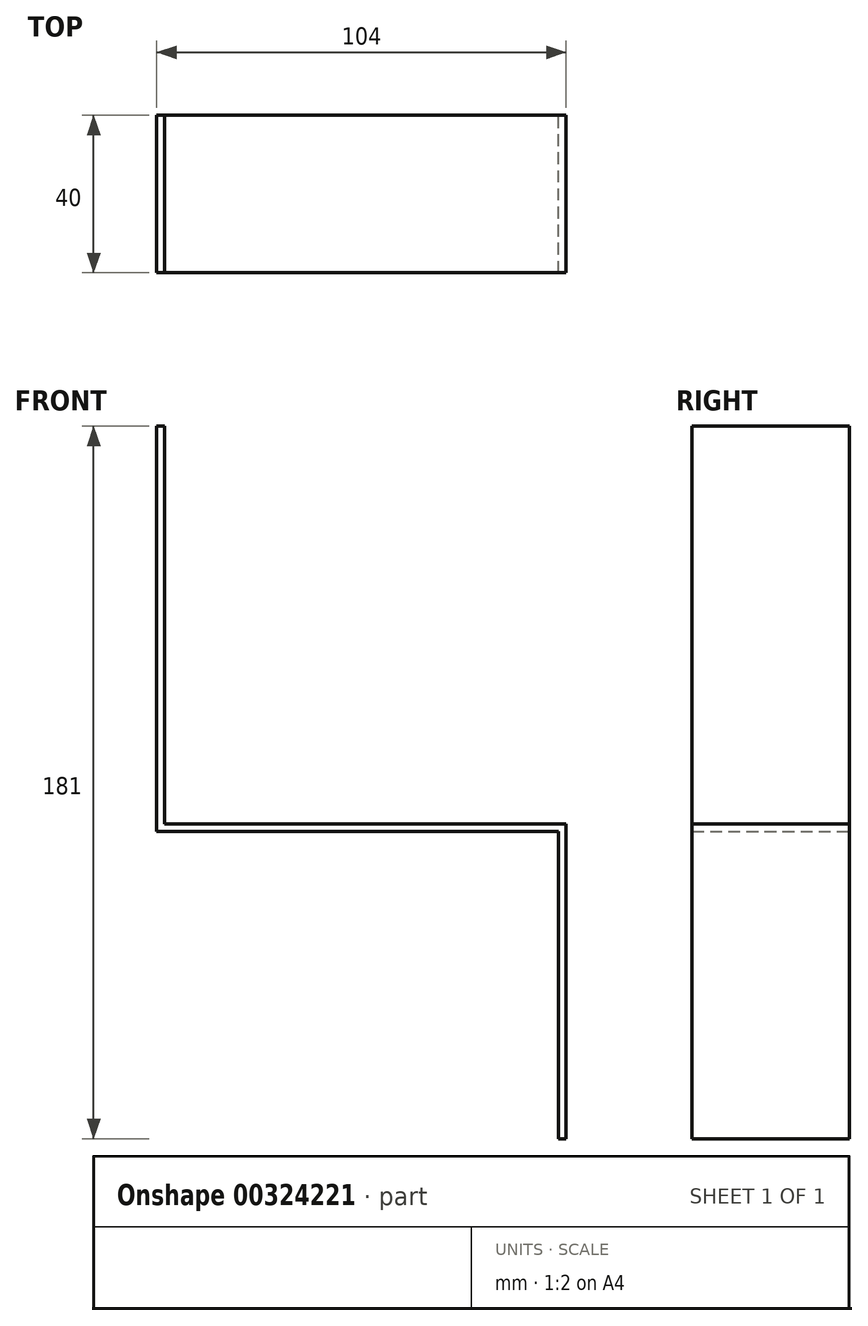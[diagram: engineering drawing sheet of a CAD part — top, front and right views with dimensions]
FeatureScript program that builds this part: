
annotation { "Feature Type Name" : "Feature", "Feature Type Description" : "" }
export const myFeature = defineFeature(function(context is Context, id is Id, definition is map)
    precondition{}
    {
        {
            var Q0;
            Q0=qCreatedBy(makeId("Front.planeOp"),FACE);
            var sketch = newSketch(context, id + "F0", { "sketchPlane" : qUnion([Q0])});
            skLineSegment(sketch, "E0", {"start": v(-47.05, 103) * mm, "end": v(-47.05, 0) * mm});
            skLineSegment(sketch, "E1", {"start": v(-47.05, 0) * mm, "end": v(54.95, 0) * mm});
            skLineSegment(sketch, "E2", {"start": v(54.95, 0) * mm, "end": v(54.95, -78) * mm});
            skLineSegment(sketch, "E3", {"start": v(54.95, -78) * mm, "end": v(56.95, -78) * mm});
            skLineSegment(sketch, "E4", {"start": v(56.95, -78) * mm, "end": v(56.95, 2) * mm});
            skLineSegment(sketch, "E5", {"start": v(56.95, 2) * mm, "end": v(-45.05, 2) * mm});
            skLineSegment(sketch, "E6", {"start": v(-45.05, 2) * mm, "end": v(-45.05, 103) * mm});
            skLineSegment(sketch, "E7", {"start": v(-45.05, 103) * mm, "end": v(-47.05, 103) * mm});
            skSolve(sketch);
        }
        {
            var Q0;
            Q0=makeQuery(id+"F0.imprint","IMPRINT",FACE,{"disambiguationData":[TD([[makeQuery(id+"F0.imprint","IMPRINT",EDGE,{"derivedFrom":sQuery(id+"F0.wireOp",EDGE,"E0")}),1.0]])]});
            extrude(context, id + "F1", {"entities" : qUnion([Q0]), "depth" : 40 * mm});
        }
    });
